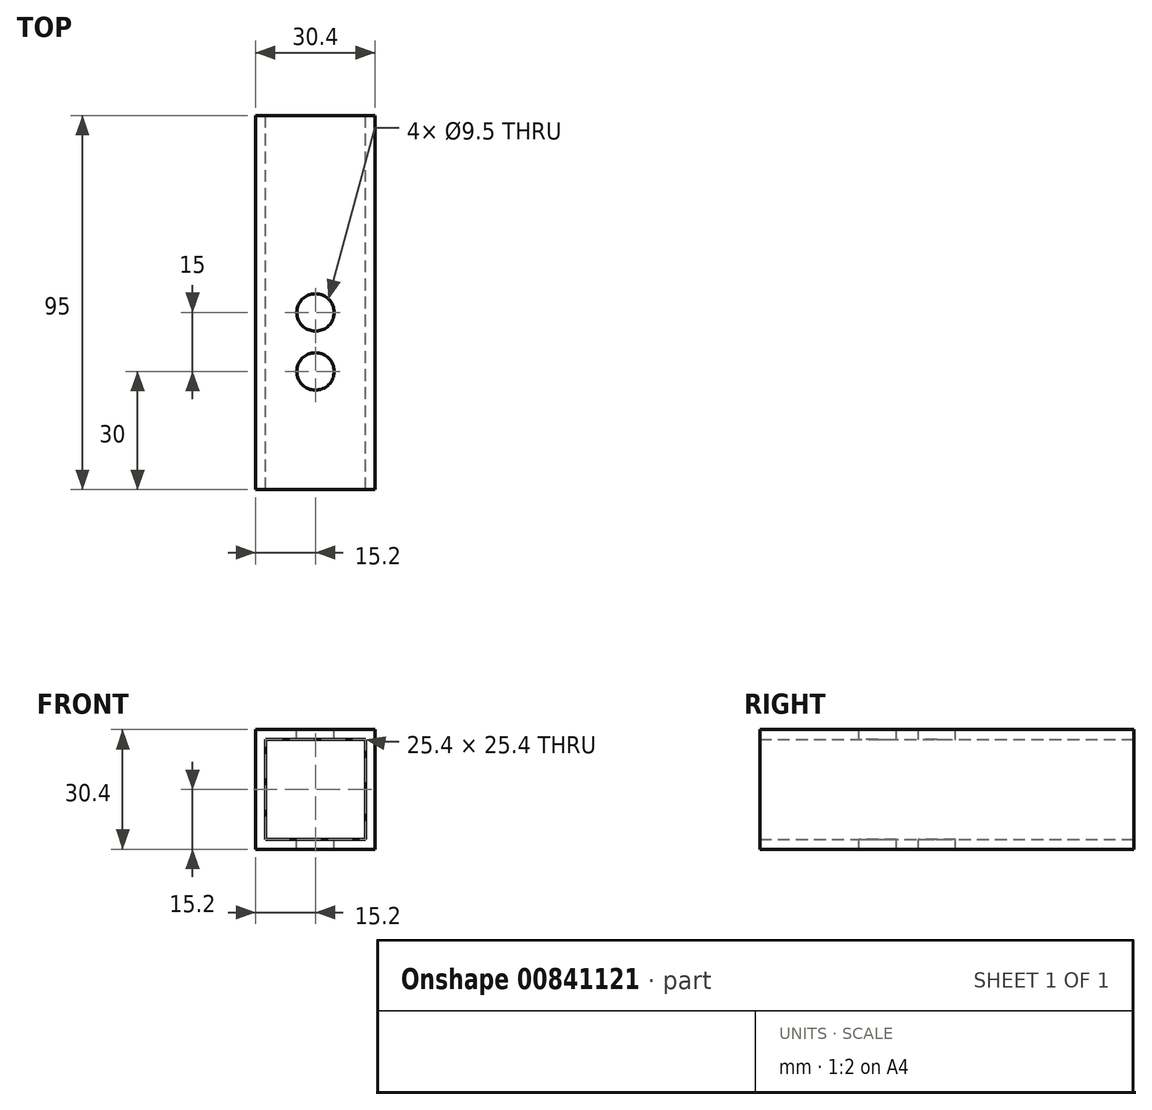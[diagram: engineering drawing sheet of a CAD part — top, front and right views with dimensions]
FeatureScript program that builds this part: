
annotation { "Feature Type Name" : "Feature", "Feature Type Description" : "" }
export const myFeature = defineFeature(function(context is Context, id is Id, definition is map)
    precondition{}
    {
        {
            var Q0;
            Q0=qCreatedBy(makeId("Front.planeOp"),FACE);
            var sketch = newSketch(context, id + "F0", { "sketchPlane" : qUnion([Q0])});
            skLineSegment(sketch, "E0.bottom", {"start": v(15.2, 15.2) * mm, "end": v(-15.2, 15.2) * mm});
            skLineSegment(sketch, "E0.top", {"start": v(15.2, -15.2) * mm, "end": v(-15.2, -15.2) * mm});
            skLineSegment(sketch, "E0.left", {"start": v(15.2, 15.2) * mm, "end": v(15.2, -15.2) * mm});
            skLineSegment(sketch, "E0.right", {"start": v(-15.2, 15.2) * mm, "end": v(-15.2, -15.2) * mm});
            skPoint(sketch, "E0.middle", {"position": v(0, 0) * mm});
            skSolve(sketch);
        }
        {
            var Q0;
            Q0=qSketchRegion(id+"F0",true);
            extrude(context, id + "F1", {"entities" : qUnion([Q0]), "depth" : 95 * mm, "offsetDistance" : 25 * mm});
        }
        {
            var Q0;
            Q0=makeQuery(id+"F1.opExtrude","CAP_FACE",FACE,{"disambiguationData":[OSD([sQuery(id+"F0.wireOp",EDGE,"E0.bottom"),sQuery(id+"F0.wireOp",EDGE,"E0.top"),sQuery(id+"F0.wireOp",EDGE,"E0.left"),sQuery(id+"F0.wireOp",EDGE,"E0.right")])],"isStart":false});
            var Q1;
            Q1=makeQuery(id+"F1.opExtrude","CAP_FACE",FACE,{"disambiguationData":[OSD([sQuery(id+"F0.wireOp",EDGE,"E0.bottom"),sQuery(id+"F0.wireOp",EDGE,"E0.top"),sQuery(id+"F0.wireOp",EDGE,"E0.left"),sQuery(id+"F0.wireOp",EDGE,"E0.right")])],"isStart":true});
            shell(context, id + "F2", {"entities" : qUnion([Q0, Q1]), "thickness" : 2.5 * mm});
        }
        {
            var Q0;
            Q0=makeQuery(id+"F1.opExtrude","SWEPT_FACE",FACE,{"disambiguationData":[OSD([sQuery(id+"F0.wireOp",EDGE,"E0.bottom")])]});
            var sketch = newSketch(context, id + "F3", { "sketchPlane" : qUnion([Q0])});
            skCircle(sketch, "E1", {"center": v(0, -50) * mm, "radius": 4.75 * mm});
            skCircle(sketch, "E2", {"center": v(0, -65) * mm, "radius": 4.75 * mm});
            skSolve(sketch);
        }
        {
            var Q0;
            Q0=makeQuery(id+"F3.imprint","IMPRINT",FACE,{"disambiguationData":[TD([[makeQuery(id+"F3.imprint","IMPRINT",EDGE,{"derivedFrom":sQuery(id+"F3.wireOp",EDGE,"E2")}),1.0]])]});
            var Q1;
            Q1=makeQuery(id+"F3.imprint","IMPRINT",FACE,{"disambiguationData":[TD([[makeQuery(id+"F3.imprint","IMPRINT",EDGE,{"derivedFrom":sQuery(id+"F3.wireOp",EDGE,"E1")}),1.0]])]});
            extrude(context, id + "F4", {"entities" : qUnion([Q0, Q1]), "operationType" : NewBodyOperationType.REMOVE, "oppositeDirection" : true, "depth" : 38.5 * mm, "offsetDistance" : 25 * mm});
        }
    });
